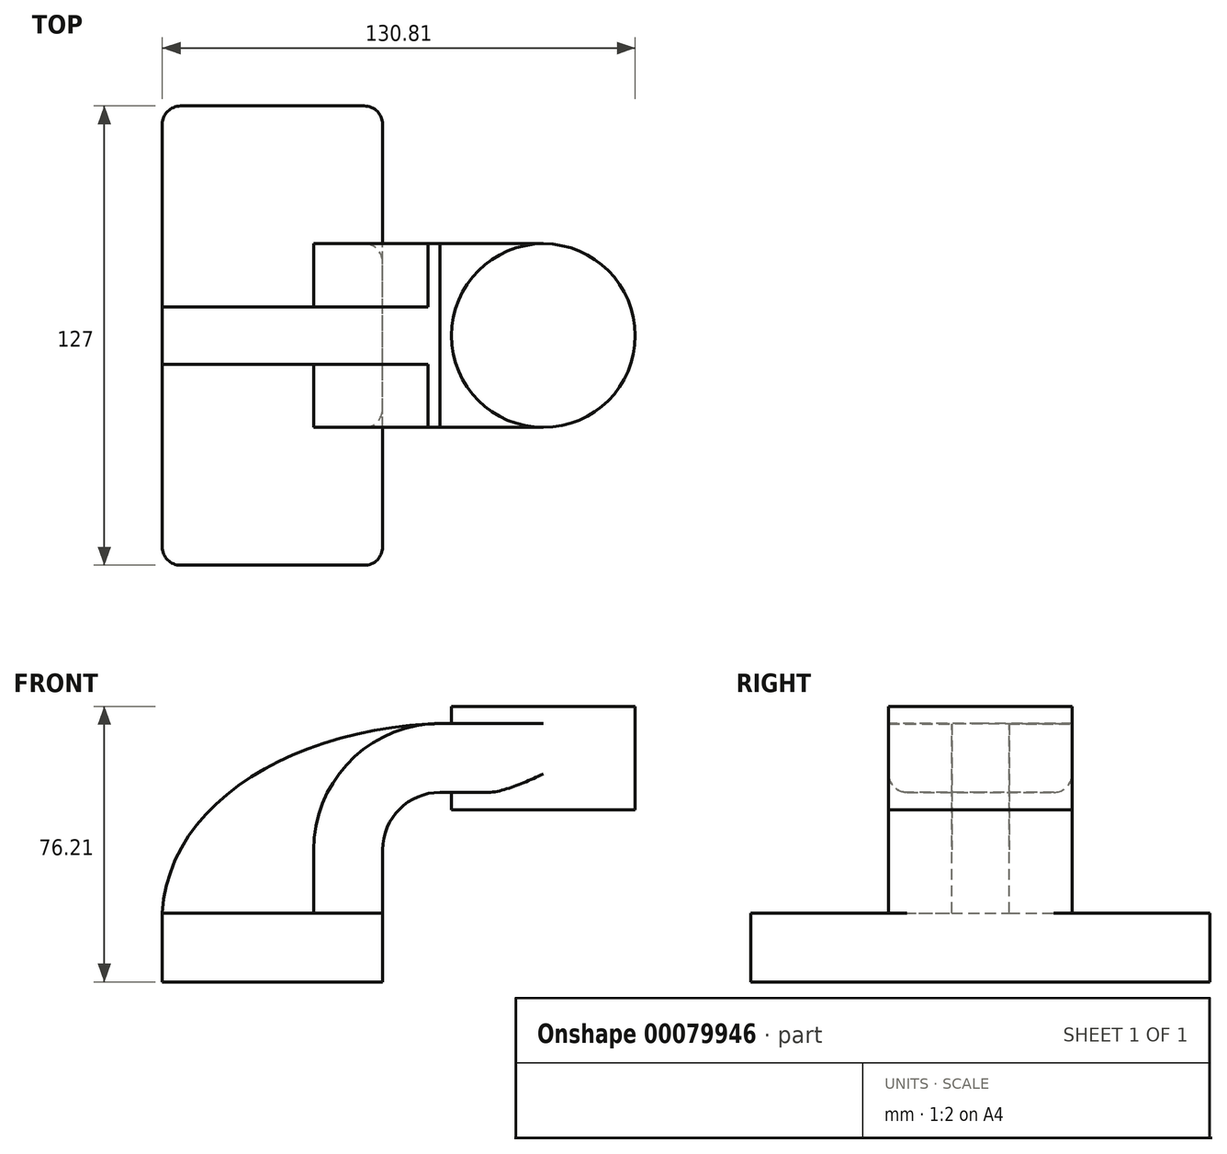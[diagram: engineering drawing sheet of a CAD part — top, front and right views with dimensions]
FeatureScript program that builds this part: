
annotation { "Feature Type Name" : "Feature", "Feature Type Description" : "" }
export const myFeature = defineFeature(function(context is Context, id is Id, definition is map)
    precondition{}
    {
        {
            var Q0;
            Q0=qCreatedBy(makeId("Front.planeOp"),FACE);
            var sketch = newSketch(context, id + "F0", { "sketchPlane" : qUnion([Q0])});
            skLineSegment(sketch, "E0.rect.bottom", {"start": v(-30.48, 9.53) * mm, "end": v(30.48, 9.53) * mm});
            skLineSegment(sketch, "E0.rect.top", {"start": v(-30.48, -9.52) * mm, "end": v(30.48, -9.52) * mm});
            skLineSegment(sketch, "E0.rect.left", {"start": v(-30.48, 9.53) * mm, "end": v(-30.48, -9.52) * mm});
            skLineSegment(sketch, "E0.rect.right", {"start": v(30.48, 9.53) * mm, "end": v(30.48, -9.52) * mm});
            skPoint(sketch, "E0.rect.middle", {"position": v(0, 0) * mm});
            skLineSegment(sketch, "E1", {"start": v(30.48, 9.53) * mm, "end": v(30.48, 27) * mm});
            skArc(sketch, "E2", {"start": v(30.48, 27) * mm, "mid": v(35.13, 38.23) * mm, "end": v(46.35, 42.88) * mm});
            skLineSegment(sketch, "E3", {"start": v(46.35, 42.88) * mm, "end": v(74.93, 42.88) * mm});
            skLineSegment(sketch, "E4.rect.bottom", {"start": v(49.53, 38.1) * mm, "end": v(100.33, 38.1) * mm});
            skLineSegment(sketch, "E4.rect.top", {"start": v(49.53, 66.67) * mm, "end": v(100.33, 66.67) * mm});
            skLineSegment(sketch, "E4.rect.left", {"start": v(49.53, 38.1) * mm, "end": v(49.53, 66.67) * mm});
            skLineSegment(sketch, "E4.rect.right", {"start": v(100.33, 38.1) * mm, "end": v(100.33, 66.68) * mm});
            skPoint(sketch, "E4.rect.middle", {"position": v(74.93, 52.39) * mm});
            skLineSegment(sketch, "E5.0", {"start": v(46.35, 61.93) * mm, "end": v(96.52, 61.93) * mm});
            skArc(sketch, "E5.1", {"start": v(11.43, 27) * mm, "mid": v(21.66, 51.7) * mm, "end": v(46.35, 61.93) * mm});
            skLineSegment(sketch, "E5.2", {"start": v(11.43, 9.52) * mm, "end": v(11.43, 27) * mm});
            skLineSegment(sketch, "E6", {"start": v(74.93, 38.1) * mm, "end": v(74.93, 66.67) * mm});
            skFitSpline(sketch, "E7", {"points": [v(-30.48, 9.53) * mm, v(46.35, 61.93) * mm], "startDerivative": vector(5.2, 92.34) * mm, "endDerivative": vector(120.92, 4.22) * mm});
            skSolve(sketch);
        }
        {
            var Q0;
            Q0=makeQuery(id+"F0.imprint","IMPRINT",FACE,{"disambiguationData":[TD([[makeQuery(id+"F0.imprint","IMPRINT",EDGE,{"derivedFrom":sQuery(id+"F0.wireOp",EDGE,"E0.rect.top")}),1.0]])]});
            extrude(context, id + "F1", {"entities" : qUnion([Q0]), "endBound" : BoundingType.SYMMETRIC, "depth" : 127 * mm});
        }
        {
            var Q0;
            {var subQ9=sQuery(id+"F0.wireOp",EDGE,"E1");Q0=makeQuery(id+"F0.imprint","IMPRINT",FACE,{"disambiguationData":[TD([[makeQuery(id+"F0.imprint","IMPRINT",EDGE,{"derivedFrom":subQ9}),1.0]])]});}
            var Q1;
            {var subQ0=sQuery(id+"F0.wireOp",EDGE,"E6");var subQ1=sQuery(id+"F0.wireOp",EDGE,"E3");var subQ2=makeQuery(id+"F0.imprint","INTERSECT",VERTEX,{"derivedFrom":[subQ1,subQ0]});Q1=makeQuery(id+"F0.imprint","IMPRINT",FACE,{"disambiguationData":[TD([[makeQuery(id+"F0.imprint","IMPRINT",EDGE,{"disambiguationData":[TD([[subQ2,1.0]])],"derivedFrom":subQ1}),1.0]])]});}
            extrude(context, id + "F2", {"entities" : qUnion([Q0, Q1]), "operationType" : NewBodyOperationType.ADD, "endBound" : BoundingType.SYMMETRIC, "depth" : 50.8 * mm});
        }
        {
            var Q0;
            {var subQ3=sQuery(id+"F0.wireOp",EDGE,"E5.2");Q0=makeQuery(id+"F0.imprint","IMPRINT",FACE,{"disambiguationData":[TD([[makeQuery(id+"F0.imprint","IMPRINT",EDGE,{"derivedFrom":subQ3}),1.0]])]});}
            extrude(context, id + "F3", {"entities" : qUnion([Q0]), "operationType" : NewBodyOperationType.ADD, "endBound" : BoundingType.SYMMETRIC, "depth" : 15.88 * mm});
        }
        {
            var Q0;
            {var subQ5=sQuery(id+"F0.wireOp",EDGE,"E4.rect.right");Q0=makeQuery(id+"F0.imprint","IMPRINT",FACE,{"disambiguationData":[TD([[makeQuery(id+"F0.imprint","IMPRINT",EDGE,{"derivedFrom":subQ5}),1.0]])]});}
            var Q1;
            Q1=sQuery(id+"F0.wireOp",EDGE,"E6");
            revolve(context, id + "F4", {"operationType" : NewBodyOperationType.ADD, "entities" : qUnion([Q0]), "axis" : qUnion([Q1]), "revolveType" : RevolveType.FULL});
        }
        {
            var Q0;
            Q0=makeQuery(id+"F1.opExtrude","CAP_EDGE",EDGE,{"disambiguationData":[OSD([sQuery(id+"F0.wireOp",EDGE,"E0.rect.right")])],"isStart":false});
            var Q1;
            Q1=makeQuery(id+"F1.opExtrude","CAP_EDGE",EDGE,{"disambiguationData":[OSD([sQuery(id+"F0.wireOp",EDGE,"E0.rect.left")])],"isStart":false});
            var Q2;
            Q2=makeQuery(id+"F1.opExtrude","CAP_EDGE",EDGE,{"disambiguationData":[OSD([sQuery(id+"F0.wireOp",EDGE,"E0.rect.right")])],"isStart":true});
            var Q3;
            Q3=makeQuery(id+"F1.opExtrude","CAP_EDGE",EDGE,{"disambiguationData":[OSD([sQuery(id+"F0.wireOp",EDGE,"E0.rect.left")])],"isStart":true});
            fillet(context, id + "F5", {"entities" : qUnion([Q0, Q1, Q2, Q3]), "radius" : 5.08 * mm, "tangentPropagation" : true, "allowEdgeOverflow" : false});
        }
        {
            var Q0;
            Q0=makeQuery(id+"F2.opExtrude","CAP_EDGE",EDGE,{"disambiguationData":[OSD([sQuery(id+"F0.wireOp",EDGE,"E3")])],"isStart":false});
            fillet(context, id + "F6", {"entities" : qUnion([Q0]), "radius" : 5.08 * mm, "tangentPropagation" : true, "allowEdgeOverflow" : false});
        }
        {
            var Q0;
            Q0=makeQuery(id+"F2.opExtrude","CAP_EDGE",EDGE,{"disambiguationData":[OSD([sQuery(id+"F0.wireOp",EDGE,"E3")])],"isStart":true});
            fillet(context, id + "F7", {"entities" : qUnion([Q0]), "radius" : 5.08 * mm, "tangentPropagation" : true, "allowEdgeOverflow" : false});
        }
    });
